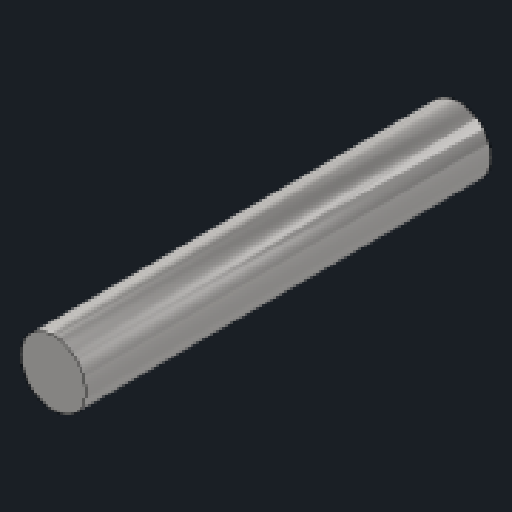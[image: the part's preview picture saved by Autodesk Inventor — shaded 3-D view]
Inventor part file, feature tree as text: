
AUTODESK INVENTOR PART (.ipt)
format: ipt  version: 2023.2 (Build 272271030, 271C)  size: 88,576 bytes
history: native  units: mm
features: extrude x1, sketch x1
ambient origin geometry x8: Origin, YZ Plane, XZ Plane, XY Plane, X Axis, Y Axis, Z Axis, Center Point
bodies: Solid1 (feature_tree)
feature tree (2):
  extrude  "Extrusion1"  Depth=29.6mm TaperAngle=0.0deg
  sketch  "Sketch1"  dims[d0=4.7625mm d1=29.6mm d2=0.0mm]
